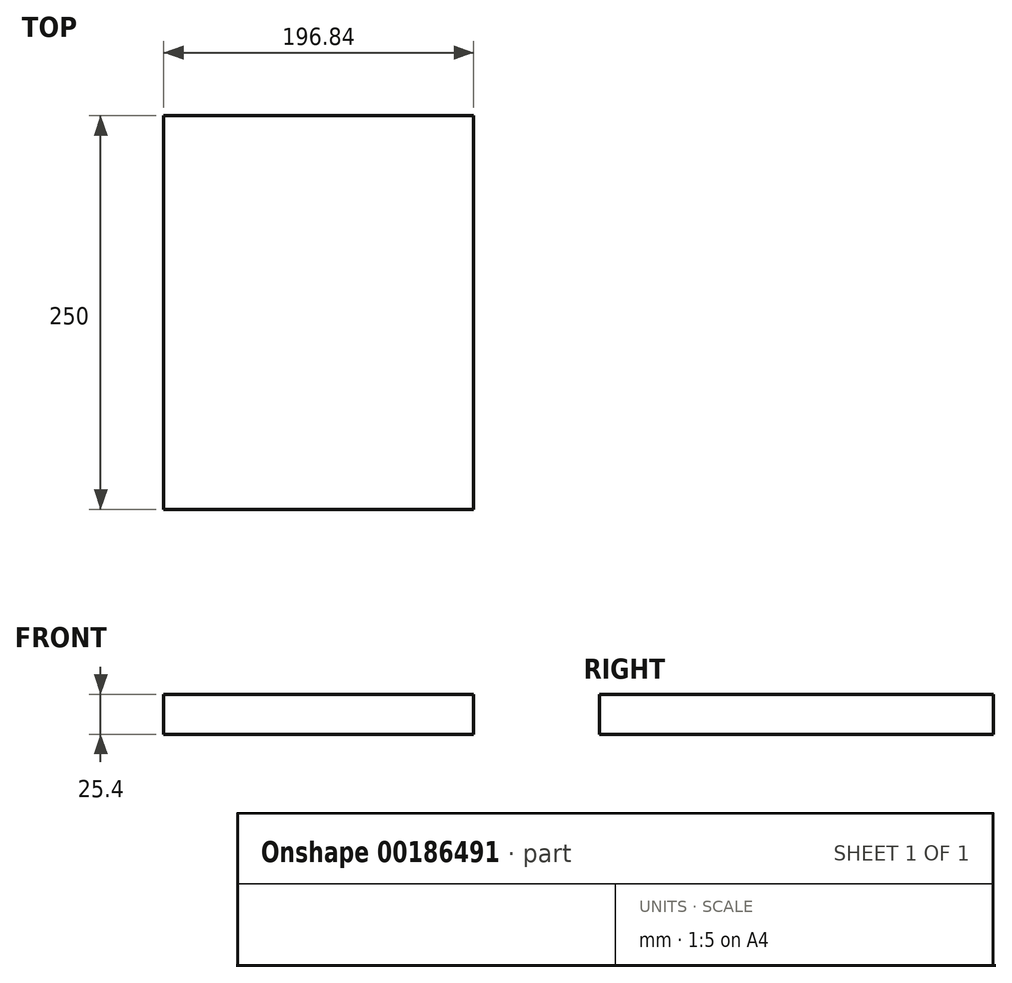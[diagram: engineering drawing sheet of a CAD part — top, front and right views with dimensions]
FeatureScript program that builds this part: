
annotation { "Feature Type Name" : "Feature", "Feature Type Description" : "" }
export const myFeature = defineFeature(function(context is Context, id is Id, definition is map)
    precondition{}
    {
        {
            var Q0;
            Q0=qCreatedBy(makeId("Top.planeOp"),FACE);
            var sketch = newSketch(context, id + "F0", { "sketchPlane" : qUnion([Q0])});
            skLineSegment(sketch, "E0.bottom", {"start": v(98.43, -125) * mm, "end": v(-98.42, -125) * mm});
            skLineSegment(sketch, "E0.top", {"start": v(98.42, 125) * mm, "end": v(-98.43, 125) * mm});
            skLineSegment(sketch, "E0.left", {"start": v(98.43, -125) * mm, "end": v(98.42, 125) * mm});
            skLineSegment(sketch, "E0.right", {"start": v(-98.42, -125) * mm, "end": v(-98.43, 125) * mm});
            skPoint(sketch, "E0.middle", {"position": v(0, 0) * mm});
            skSolve(sketch);
        }
        {
            var Q0;
            Q0 = qSketchRegion(id + "F0", true);
            extrude(context, id + "F1", {"entities" : qUnion([Q0]), "depth" : 25.4 * mm});
        }
    });
